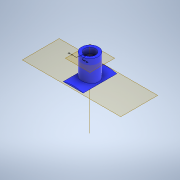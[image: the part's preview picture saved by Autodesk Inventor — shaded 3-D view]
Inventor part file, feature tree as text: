
AUTODESK INVENTOR PART (.ipt)
format: ipt  version: 2021 (Build 250183000, 183)  size: 204,288 bytes
history: native  units: in
note: dims shown in document units (in); Inventor stores cm internally (conversion verified against a paired STEP export)
features: sketch x7, extrude x6, other x3, plane x2, hole x1, mirror x1
ambient origin geometry x8: Origin, YZ Plane, XZ Plane, XY Plane, X Axis, Y Axis, Z Axis, Center Point
bodies: Body1 (feature_tree)
feature tree (20):
  other  "Annotations"
  extrude  "Extrusion5"  Depth=0.25in
  hole  "Hole3"  [1 undecoded]
  mirror  "Mirror3"
  plane  "Work Plane7"
  extrude  "Extrusion11"  Depth=3.0in TaperAngle=0.0deg
  extrude  "Extrusion13"  Depth=1.0in
  extrude  "Extrusion14"  Depth=3.125in
  plane  "Work Plane9"
  extrude  "Extrusion15"  Depth=1.5in TaperAngle=0.0deg
  extrude  "Extrusion16"  Depth=0.75in TaperAngle=0.0deg
  sketch  "Sketch8"  dims[d52=6.0in d53=0.25in]
  sketch  "Sketch9"  dims[d54=0.75in d55=0.125in]
  sketch  "Sketch20"  dims[d56=0.25in d57=3.0in d58=0.0in]
  sketch  "Sketch22"  dims[d59=0.5in d60=1.1811in d62=1.0in d63=0.3937in d65=1.0in]
  sketch  "Sketch23"  dims[d67=0.266in d68=0.75in d69=0.438in d70=0.25in d71=0.5635in d72=1.0in d73=0.8108in d100=3.125in]
  sketch  "Sketch24"  dims[d101=1.5in d102=2.0in d103=0.0in]
  sketch  "Sketch25"  dims[d111=1.0in d112=2.0in d113=0.0in d114=1.125in d115=0.0625in d116=0.0625in d117=1.0in d118=0.5in d119=0.0in d120=-0.5in d121=1.125in d122=0.5in d123=0.0in d128=3.0in d129=0.0in d124=3.0003in d125=1.0in d126=0.0in d127=1.125in d11=1.0in d12=1.0in d13=1.0in d14=0.15in d15=0.25in d16=0.375in d17=0.5635in d18=0.75in d19=0.8108in d20=0.0625in d21=0.75in d22=0.375in]
  other  "Diameter Dimension 1"
  other  "Diameter Dimension 2"
note: 1 required parameter value undecoded (feature->parameter linkage not recoverable at this tier; creation-order binding heuristic only, values carry confidence <= 0.55)
